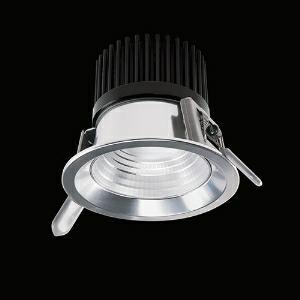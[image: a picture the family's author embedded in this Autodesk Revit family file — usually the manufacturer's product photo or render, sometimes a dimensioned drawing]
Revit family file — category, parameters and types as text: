
# Revit family: spectral_myral_myral_1500-830-m-dali
name_source: partatom
category: Lighting Fixtures
revit_build: Autodesk Revit 2016 (Build: 20150220_1215(x64)
units: mm (PartAtom-declared; Revit-internal decimal feet)

## family parameters
Cut with Voids When Loaded = No
Host = Face
Light Source = No
Part Type = Normal
Room Calculation Point = No
Round Connector Dimension = Use Diameter
Shared = No

## types (1)
- SPECTRAL MYRAL (1 x )
    Apparent Load = 0 VA
    Approval mark = CE
    CIE Flux Codes = 82 99 100 100 100
    Control Gear = Electronic transformer
    Default Elevation = 1800 mm
    Description = SPG0330178
MYRAL recessed spot

Design:
    Height = 0 mm  [stored 0 ft]
    Lamp = 1 x
    Lamp count = 1
    Length = 120 mm
    Luminous efficacy = 0 lm/W
    Manufacturer = Ridi
    ModVariant = No
    Model = MYRAL 1500-830-M-DALI
    Mounting Place = Ceiling
    Mounting Type = Recessed
    Number of Poles = 1
    OnlyDefault = Yes
    Power Factor = 1
    Product Name = SPECTRAL MYRAL
    Product group = Downlight recessed
    ProductGroupID = 400
    Protection Class = Protection class
    Protection Degree = IP 20
    RlxData = <blob elided: 38657 chars, md5=1754d622>
    Socket = socket
    Standby Power = 0 W
    System Light Flux = 0 lm
    System Power = 0 W
    Type Image = myral_04.jpg
    URL = http://reluxnet.relux.com
    VarID = ---
    Voltage = 0 V
    Weight = 0.00 kg
    Width = 0 mm  [stored 0 ft]

note: [stored X ft] marks values corroborated as IEEE doubles in the binary element streams (Revit-internal decimal feet)

## geometry (parser evidence)
native form markers: Sweep x8
no freeform markers — native parametric forms only
